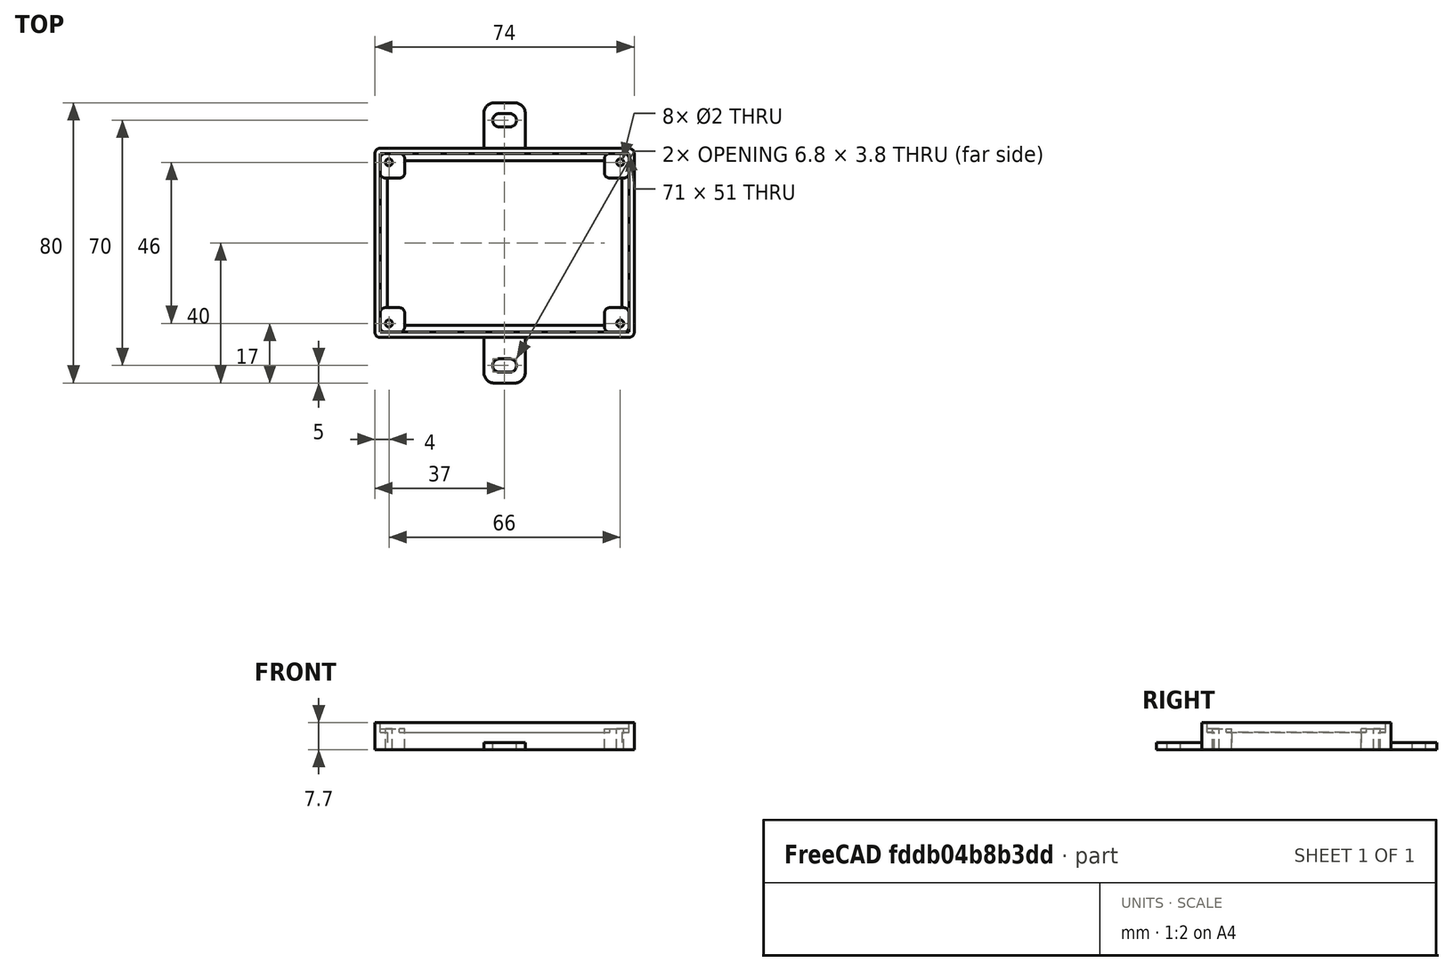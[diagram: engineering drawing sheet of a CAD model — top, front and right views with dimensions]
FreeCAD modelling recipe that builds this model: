
FCSTD DOCUMENT  (FreeCAD 0.19R)
Label: pcb_7x5
License: All rights reserved
LicenseURL: http://en.wikipedia.org/wiki/All_rights_reserved
objects: Part::Box×8, Part::MultiFuse×5, Part::Cut×5, Part::FeaturePython×4, Part::Fillet×4, App::Part×3, Part::Cylinder×2, Spreadsheet::Sheet×1, Part::Feature×1, PartDesign::FeatureBase×1, PartDesign::Body×1
note: 31 computed .brp shape members not serialized (recipe doc carries the construction recipe); baked Part::Feature solids carry a one-line shape summary decoded from their .brp

FEATURE [Spreadsheet::Sheet] Spreadsheet  label="p"
  cells = A1=hole_x_dist; B1(hole_x_dist)=64; A2=hole_y_dist; B2(hole_y_dist)=44; A3=dd_hole_x_dist; B3(dd_hole_x_dist)=66; A4=dd_hole_y_dist; B4(dd_hole_y_dist)=46; A5=pcb_under; B5(pcb_under)=3; A6=pcb_x; B6(pcb_x)=71; A7=pcb_y; B7(pcb_y)=51; A8=hole_stand_x; B8(hole_stand_x)=7; A9=hole_stand_y; B9(hole_stand_y)=7; A10=hole_r; B10(hole_r)=1; A11=box_wall; B11(box_wall)=1.5; A12=under_layer; B12(under_layer)=3; A13=pcb_height; B13(pcb_height)=1.7; A14=under_pcb_border; B14(under_pcb_border)=2
FEATURE [Part::Box] Box  label="bottom cube"
  AttacherType = Attacher::AttachEngine3D
  Height = 7.7
  Length = 74
  Width = 54
  expr: Width = <<p>>.pcb_y + <<p>>.box_wall * 2
  expr: Length = <<p>>.pcb_x + <<p>>.box_wall * 2
  expr: Height = <<p>>.pcb_under + <<p>>.pcb_height + <<p>>.under_layer
FEATURE [Part::Box] Box001  label="bottom extraction"
  AttacherType = Attacher::AttachEngine3D
  Height = 10
  Length = 67
  Placement = pos=(3.5,3.5,0) rot=(0,0,1;0rad)
  Width = 47
  expr: .Placement.Base.y = <<p>>.under_pcb_border + <<p>>.box_wall
  expr: .Placement.Base.x = <<p>>.under_pcb_border + <<p>>.box_wall
  expr: Length = <<p>>.pcb_x - <<p>>.under_pcb_border * 2
  expr: Width = <<p>>.pcb_y - <<p>>.under_pcb_border * 2
FEATURE [Part::Box] Box002  label="pcb extraction"
  AttacherType = Attacher::AttachEngine3D
  Height = 10
  Length = 71
  Placement = pos=(1.5,1.5,5) rot=(0,0,1;0rad)
  Width = 51
  expr: .Placement.Base.z = <<p>>.under_pcb_border + <<p>>.under_layer
  expr: .Placement.Base.y = <<p>>.box_wall
  expr: .Placement.Base.x = <<p>>.box_wall
  expr: Length = <<p>>.pcb_x
  expr: Width = <<p>>.pcb_y
FEATURE [Part::MultiFuse] Fusion  label="bottom extraction001"
  Shapes = -> [Box001,Box002]
FEATURE [Part::Box] Box003  label="hole stand cube"
  AttacherType = Attacher::AttachEngine3D
  Height = 6
  Length = 7
  Placement = pos=(1.5,1.5,0) rot=(0,0,1;0rad)
  Width = 7
  expr: .Placement.Base.y = <<p>>.box_wall
  expr: .Placement.Base.x = <<p>>.box_wall
  expr: Height = <<p>>.pcb_under + <<p>>.under_layer
  expr: Width = <<p>>.hole_stand_y
  expr: Length = <<p>>.hole_stand_x
FEATURE [Part::Cylinder] Cylinder  label="pcb hole"
  Angle = 360
  AttacherType = Attacher::AttachEngine3D
  Height = 10
  Placement = pos=(5,5,0) rot=(0,0,1;0rad)
  Radius = 1
  expr: .Placement.Base.y = (<<p>>.box_wall * 2 + <<p>>.pcb_y - <<p>>.hole_y_dist) / 2
  expr: .Placement.Base.x = (<<p>>.box_wall * 2 + <<p>>.pcb_x - <<p>>.hole_x_dist) / 2
  expr: Radius = <<p>>.hole_r
FEATURE [Part::FeaturePython] Array001  label="hole array"  # Draft array (typed FeaturePython)
  Angle = 360
  ArrayType = 0
  Axis = (0,0,1)
  Base = -> Cylinder
  Center = (0,0,0)
  Fuse = false
  IntervalAxis = (0,0,0)
  IntervalX = (64,0,0)
  IntervalY = (0,44,0)
  IntervalZ = (0,0,1)
  NumberPolar = 1
  NumberX = 2
  NumberY = 2
  NumberZ = 1
  expr: .IntervalY.y = <<p>>.hole_y_dist
  expr: .IntervalX.x = <<p>>.hole_x_dist
FEATURE [Part::Fillet] Fillet001  label="bottom cube fillet"
  Base = -> Box
  Edges = 4 edges r=1.5: [Edge1,Edge3,Edge5,Edge7]
FEATURE [Part::Feature] Cut002002  label="attach plane y dir002"
  Placement = pos=(31.1,-13,0) rot=(0,0,1;0rad)
  shape: bbox 11.8 x 80 x 2 mm, 20 faces (baked)
FEATURE [Part::MultiFuse] Fusion002  label="bottom fusion"
  Shapes = -> [Fillet001,Cut002002]
FEATURE [Part::Cut] Cut  label="pcb box cut"
  Base = -> Fusion002
  Tool = -> Fusion
FEATURE [Part::Cylinder] Cylinder002  label="dd pcb hole"
  Angle = 360
  AttacherType = Attacher::AttachEngine3D
  Height = 10
  Placement = pos=(4,4,0) rot=(0,0,1;0rad)
  Radius = 1
  expr: Radius = <<p>>.hole_r
  expr: .Placement.Base.x = (<<p>>.box_wall * 2 + <<p>>.pcb_x - <<p>>.dd_hole_x_dist) / 2
  expr: .Placement.Base.y = (<<p>>.box_wall * 2 + <<p>>.pcb_y - <<p>>.dd_hole_y_dist) / 2
FEATURE [Part::FeaturePython] Array005  label="dd hole array"  # Draft array (typed FeaturePython)
  Angle = 360
  ArrayType = 0
  Axis = (0,0,1)
  Base = -> Cylinder002
  Center = (0,0,0)
  Fuse = false
  IntervalAxis = (0,0,0)
  IntervalX = (66,0,0)
  IntervalY = (0,46,0)
  IntervalZ = (0,0,1)
  NumberPolar = 1
  NumberX = 2
  NumberY = 2
  NumberZ = 1
  expr: .IntervalX.x = <<p>>.dd_hole_x_dist
  expr: .IntervalY.y = <<p>>.dd_hole_y_dist
FEATURE [Part::Fillet] Fillet  label="stand fillet"
  Base = -> Box003
  Edges = 4 edges r=1.5: [Edge1,Edge3,Edge5,Edge7]
FEATURE [Part::FeaturePython] Array  label="hole stand array"  # Draft array (typed FeaturePython)
  Angle = 360
  ArrayType = 0
  Axis = (0,0,1)
  Base = -> Fillet
  Center = (0,0,0)
  Fuse = false
  IntervalAxis = (0,0,0)
  IntervalX = (64,0,0)
  IntervalY = (0,44,0)
  IntervalZ = (0,0,1)
  NumberPolar = 1
  NumberX = 2
  NumberY = 2
  NumberZ = 1
  expr: .IntervalY.y = <<p>>.pcb_y - <<p>>.hole_stand_y
  expr: .IntervalX.x = <<p>>.pcb_x - <<p>>.hole_stand_x
FEATURE [Part::MultiFuse] Fusion001  label="frame fusion"
  Shapes = -> [Array,Cut]
FEATURE [Part::Cut] Cut001  label="frame fusion with holes"
  Base = -> Fusion001
  Tool = -> Array001
FEATURE [App::Part] Part  label="pcb with 4 holes siggle layer part"
  Group = -> [Fusion,Fusion002,Box002,Box001,Array001,Cut,Array,Cylinder,Fusion001,Cut001]
  Origin = -> Origin
FEATURE [PartDesign::FeatureBase] Clone
  BaseFeature = -> Fusion001
FEATURE [PartDesign::Body] Body  label="frame fusion clone"
  BaseFeature = -> Fusion001
  Group = -> [Clone]
  Origin = -> Origin003
  Tip = -> Clone
FEATURE [Part::Cut] Cut002003  label="dd frame fusion with holes"
  Base = -> Body
  Tool = -> Array005
FEATURE [App::Part] Part001  label="pcb with 4 holes double layer part"
  Group = -> [Body,Cylinder002,Array005,Cut002003]
  Origin = -> Origin002
FEATURE [Part::Box] Box004  label="bottom extraction002"
  AttacherType = Attacher::AttachEngine3D
  Height = 10
  Length = 67
  Placement = pos=(3.5,3.5,0) rot=(0,0,1;0rad)
  Width = 47
  expr: Width = <<p>>.pcb_y - <<p>>.under_pcb_border * 2
  expr: Length = <<p>>.pcb_x - <<p>>.under_pcb_border * 2
  expr: .Placement.Base.x = <<p>>.under_pcb_border + <<p>>.box_wall
  expr: .Placement.Base.y = <<p>>.under_pcb_border + <<p>>.box_wall
FEATURE [Part::Box] Box005  label="pcb extraction001"
  AttacherType = Attacher::AttachEngine3D
  Height = 10
  Length = 71
  Placement = pos=(1.5,1.5,5) rot=(0,0,1;0rad)
  Width = 51
  expr: Width = <<p>>.pcb_y
  expr: Length = <<p>>.pcb_x
  expr: .Placement.Base.x = <<p>>.box_wall
  expr: .Placement.Base.y = <<p>>.box_wall
  expr: .Placement.Base.z = <<p>>.under_pcb_border + <<p>>.under_layer
FEATURE [Part::Box] Box006  label="hole stand cube001"
  AttacherType = Attacher::AttachEngine3D
  Height = 6
  Length = 7
  Placement = pos=(1.5,1.5,0) rot=(0,0,1;0rad)
  Width = 7
  expr: Length = <<p>>.hole_stand_x
  expr: Width = <<p>>.hole_stand_y
  expr: Height = <<p>>.pcb_under + <<p>>.under_layer
  expr: .Placement.Base.x = <<p>>.box_wall
  expr: .Placement.Base.y = <<p>>.box_wall
FEATURE [Part::Fillet] Fillet002  label="stand fillet001"
  Base = -> Box006
  Edges = 4 edges r=1.5: [Edge1,Edge3,Edge5,Edge7]
FEATURE [Part::FeaturePython] Array007  label="hole stand array001"  # Draft array (typed FeaturePython)
  Angle = 360
  ArrayType = 0
  Axis = (0,0,1)
  Base = -> Fillet002
  Center = (0,0,0)
  Fuse = false
  IntervalAxis = (0,0,0)
  IntervalX = (64,0,0)
  IntervalY = (0,44,0)
  IntervalZ = (0,0,1)
  NumberPolar = 1
  NumberX = 2
  NumberY = 2
  NumberZ = 1
  expr: .IntervalX.x = <<p>>.pcb_x - <<p>>.hole_stand_x
  expr: .IntervalY.y = <<p>>.pcb_y - <<p>>.hole_stand_y
FEATURE [Part::MultiFuse] Fusion005  label="bottom extraction003"
  Shapes = -> [Box004,Box005]
FEATURE [Part::Box] Box007  label="bottom cube001"
  AttacherType = Attacher::AttachEngine3D
  Height = 7.7
  Length = 74
  Width = 54
  expr: Height = <<p>>.pcb_under + <<p>>.pcb_height + <<p>>.under_layer
  expr: Length = <<p>>.pcb_x + <<p>>.box_wall * 2
  expr: Width = <<p>>.pcb_y + <<p>>.box_wall * 2
FEATURE [Part::Fillet] Fillet003  label="bottom cube fillet001"
  Base = -> Box007
  Edges = 4 edges r=1.5: [Edge1,Edge3,Edge5,Edge7]
FEATURE [Part::Cut] Cut002004  label="pcb box cut001"
  Base = -> Fillet003
  Tool = -> Fusion005
FEATURE [Part::MultiFuse] Fusion003  label="frame fusion001"
  Shapes = -> [Array007,Cut002004]
FEATURE [Part::Cut] Cut002005  label="dd frame fusion with holes no attachment"
  Base = -> Fusion003
  Tool = -> Array005
FEATURE [App::Part] Part002  label="pcb with 4 holes double layer no attachment"
  Group = -> [Fusion005,Box005,Box004,Cut002004,Array007,Fusion003,Cut002005]
  Origin = -> Origin004
